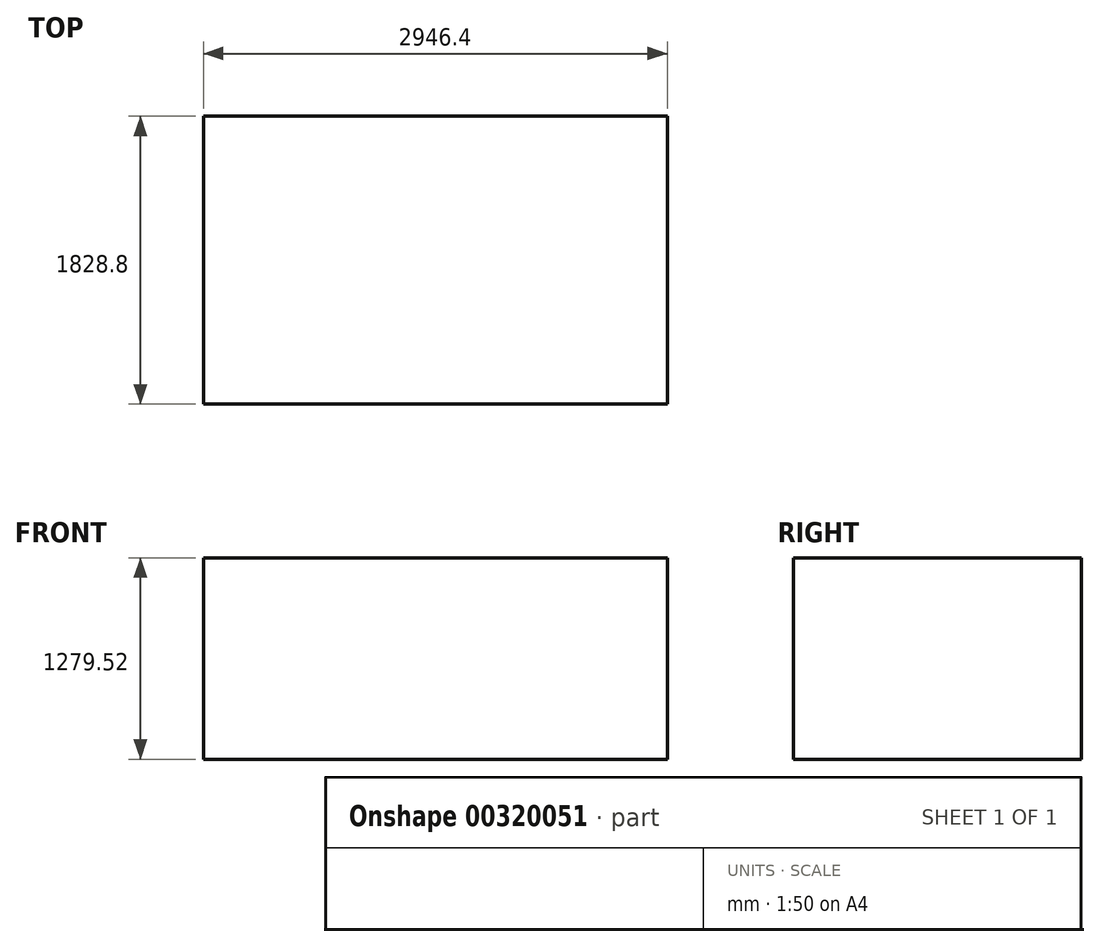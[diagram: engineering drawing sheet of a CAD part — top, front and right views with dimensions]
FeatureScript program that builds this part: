
annotation { "Feature Type Name" : "Feature", "Feature Type Description" : "" }
export const myFeature = defineFeature(function(context is Context, id is Id, definition is map)
    precondition{}
    {
        {
            var Q0;
            Q0=qCreatedBy(makeId("Front.planeOp"),FACE);
            var sketch = newSketch(context, id + "F0", { "sketchPlane" : qUnion([Q0])});
            skLineSegment(sketch, "E0", {"start": v(-1473.2, -944.56) * mm, "end": v(-1473.2, 334.96) * mm});
            skLineSegment(sketch, "E1", {"start": v(-1473.2, 334.96) * mm, "end": v(1473.2, 334.96) * mm});
            skLineSegment(sketch, "E2", {"start": v(1473.2, 334.96) * mm, "end": v(1473.2, -944.56) * mm});
            skLineSegment(sketch, "E3", {"start": v(1473.2, -944.56) * mm, "end": v(-1473.2, -944.56) * mm});
            skSolve(sketch);
        }
        {
            var Q0;
            {var subQ3=sQuery(id+"F0.wireOp",EDGE,"E0");Q0=makeQuery(id+"F0.imprint","IMPRINT",FACE,{"disambiguationData":[TD([[makeQuery(id+"F0.imprint","IMPRINT",EDGE,{"derivedFrom":subQ3}),-1.0]])]});}
            extrude(context, id + "F1", {"entities" : qUnion([Q0]), "endBound" : BoundingType.SYMMETRIC, "depth" : 1828.8 * mm});
        }
    });
